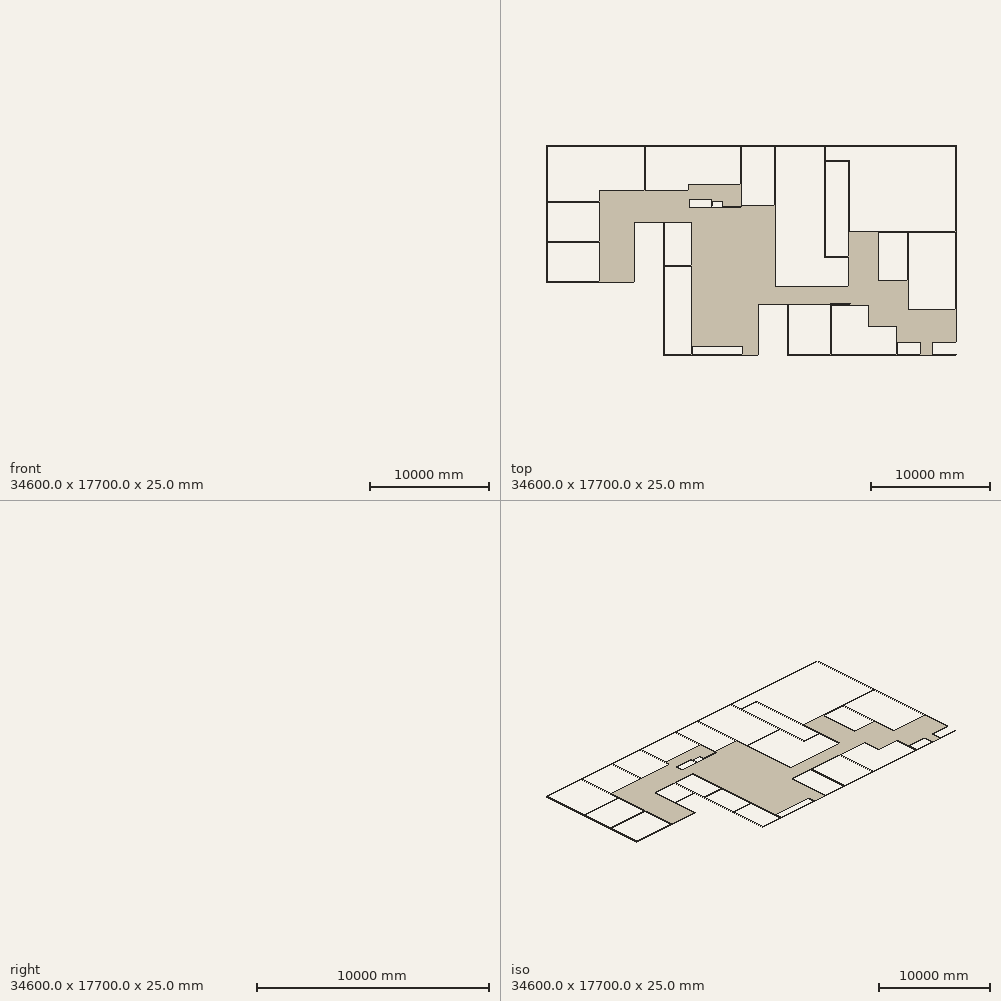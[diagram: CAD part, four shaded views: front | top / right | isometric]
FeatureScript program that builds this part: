
annotation { "Feature Type Name" : "Feature", "Feature Type Description" : "" }
export const myFeature = defineFeature(function(context is Context, id is Id, definition is map)
    precondition{}
    {
        {
            var Q0;
            Q0=qCreatedBy(makeId("Top.planeOp"),FACE);
            var sketch = newSketch(context, id + "F0", { "sketchPlane" : qUnion([Q0])});
            skLineSegment(sketch, "E0", {"start": v(-12169.64, -2200) * mm, "end": v(-12169.64, 9350) * mm});
            skLineSegment(sketch, "E1", {"start": v(-12169.64, 9350) * mm, "end": v(22430.36, 9350) * mm});
            skLineSegment(sketch, "E2", {"start": v(22430.36, 9350) * mm, "end": v(22430.36, -8350) * mm});
            skLineSegment(sketch, "E3", {"start": v(22430.36, -8350) * mm, "end": v(-2269.64, -8350) * mm});
            skLineSegment(sketch, "E4", {"start": v(-2269.64, -8350) * mm, "end": v(-2269.64, 300) * mm});
            skLineSegment(sketch, "E5", {"start": v(-2269.64, 300) * mm, "end": v(-4769.64, 300) * mm});
            skLineSegment(sketch, "E6", {"start": v(-4769.64, 300) * mm, "end": v(-4769.64, -2200) * mm});
            skLineSegment(sketch, "E7", {"start": v(-4769.64, -2200) * mm, "end": v(-12169.64, -2200) * mm});
            skLineSegment(sketch, "E8.bottom", {"start": v(-12119.64, 9300) * mm, "end": v(-7719.64, 9300) * mm});
            skLineSegment(sketch, "E8.top", {"start": v(-12119.64, 4600) * mm, "end": v(-7719.64, 4600) * mm});
            skLineSegment(sketch, "E8.left", {"start": v(-12119.64, 9300) * mm, "end": v(-12119.64, 4600) * mm});
            skLineSegment(sketch, "E8.right", {"start": v(-7719.64, 9300) * mm, "end": v(-7719.64, 4600) * mm});
            skLineSegment(sketch, "E9.bottom", {"start": v(-7669.64, 9300) * mm, "end": v(-3869.64, 9300) * mm});
            skLineSegment(sketch, "E9.top", {"start": v(-7669.64, 5600) * mm, "end": v(-3869.64, 5600) * mm});
            skLineSegment(sketch, "E9.left", {"start": v(-7669.64, 9300) * mm, "end": v(-7669.64, 5600) * mm});
            skLineSegment(sketch, "E9.right", {"start": v(-3869.64, 9300) * mm, "end": v(-3869.64, 5600) * mm});
            skLineSegment(sketch, "E10.bottom", {"start": v(-3819.64, 9300) * mm, "end": v(-219.64, 9300) * mm});
            skLineSegment(sketch, "E10.top", {"start": v(-3819.64, 5600) * mm, "end": v(-219.64, 5600) * mm});
            skLineSegment(sketch, "E10.left", {"start": v(-3819.64, 9300) * mm, "end": v(-3819.64, 5600) * mm});
            skLineSegment(sketch, "E10.right", {"start": v(-219.64, 9300) * mm, "end": v(-219.64, 5600) * mm});
            skLineSegment(sketch, "E11.bottom", {"start": v(-12119.64, 1175) * mm, "end": v(-7719.64, 1175) * mm});
            skLineSegment(sketch, "E11.top", {"start": v(-12119.64, -2150) * mm, "end": v(-7719.64, -2150) * mm});
            skLineSegment(sketch, "E11.left", {"start": v(-12119.64, 1175) * mm, "end": v(-12119.64, -2150) * mm});
            skLineSegment(sketch, "E11.right", {"start": v(-7719.64, 1175) * mm, "end": v(-7719.64, -2150) * mm});
            skLineSegment(sketch, "E12.bottom", {"start": v(-12119.64, 4550) * mm, "end": v(-7719.64, 4550) * mm});
            skLineSegment(sketch, "E12.top", {"start": v(-12119.64, 1225) * mm, "end": v(-7719.64, 1225) * mm});
            skLineSegment(sketch, "E12.left", {"start": v(-12119.64, 4550) * mm, "end": v(-12119.64, 1225) * mm});
            skLineSegment(sketch, "E12.right", {"start": v(-7719.64, 4550) * mm, "end": v(-7719.64, 1225) * mm});
            skLineSegment(sketch, "E13.bottom", {"start": v(-169.64, 9300) * mm, "end": v(4230.36, 9300) * mm});
            skLineSegment(sketch, "E13.top", {"start": v(-169.64, 6100) * mm, "end": v(4230.36, 6100) * mm});
            skLineSegment(sketch, "E13.left", {"start": v(-169.64, 9300) * mm, "end": v(-169.64, 6100) * mm});
            skLineSegment(sketch, "E13.right", {"start": v(4230.36, 9300) * mm, "end": v(4230.36, 6100) * mm});
            skLineSegment(sketch, "E14.bottom", {"start": v(4280.36, 9300) * mm, "end": v(7080.36, 9300) * mm});
            skLineSegment(sketch, "E14.top", {"start": v(4280.36, 4300) * mm, "end": v(7080.36, 4300) * mm});
            skLineSegment(sketch, "E14.left", {"start": v(4280.36, 9300) * mm, "end": v(4280.36, 4300) * mm});
            skLineSegment(sketch, "E14.right", {"start": v(7080.36, 9300) * mm, "end": v(7080.36, 4300) * mm});
            skLineSegment(sketch, "E15.bottom", {"start": v(-129.64, 4190) * mm, "end": v(4270.36, 4190) * mm});
            skLineSegment(sketch, "E15.top", {"start": v(-129.64, 4090) * mm, "end": v(4270.36, 4090) * mm});
            skLineSegment(sketch, "E15.left", {"start": v(-129.64, 4190) * mm, "end": v(-129.64, 4090) * mm});
            skLineSegment(sketch, "E15.right", {"start": v(4270.36, 4190) * mm, "end": v(4270.36, 4090) * mm});
            skLineSegment(sketch, "E16.bottom", {"start": v(-2219.64, -4600) * mm, "end": v(80.36, -4600) * mm});
            skLineSegment(sketch, "E16.top", {"start": v(-2219.64, -8300) * mm, "end": v(80.36, -8300) * mm});
            skLineSegment(sketch, "E16.left", {"start": v(-2219.64, -4600) * mm, "end": v(-2219.64, -8300) * mm});
            skLineSegment(sketch, "E16.right", {"start": v(80.36, -4600) * mm, "end": v(80.36, -8300) * mm});
            skLineSegment(sketch, "E17.bottom", {"start": v(-2219.64, -850) * mm, "end": v(80.36, -850) * mm});
            skLineSegment(sketch, "E17.top", {"start": v(-2219.64, -4550) * mm, "end": v(80.36, -4550) * mm});
            skLineSegment(sketch, "E17.left", {"start": v(-2219.64, -850) * mm, "end": v(-2219.64, -4550) * mm});
            skLineSegment(sketch, "E17.right", {"start": v(80.36, -850) * mm, "end": v(80.36, -4550) * mm});
            skLineSegment(sketch, "E18.bottom", {"start": v(-2219.64, 2900) * mm, "end": v(80.36, 2900) * mm});
            skLineSegment(sketch, "E18.top", {"start": v(-2219.64, -800) * mm, "end": v(80.36, -800) * mm});
            skLineSegment(sketch, "E18.left", {"start": v(-2219.64, 2900) * mm, "end": v(-2219.64, -800) * mm});
            skLineSegment(sketch, "E18.right", {"start": v(80.36, 2900) * mm, "end": v(80.36, -800) * mm});
            skLineSegment(sketch, "E19.bottom", {"start": v(7130.36, 9300) * mm, "end": v(11330.36, 9300) * mm});
            skLineSegment(sketch, "E19.top", {"start": v(7130.36, 3050) * mm, "end": v(11330.36, 3050) * mm});
            skLineSegment(sketch, "E19.left", {"start": v(7130.36, 9300) * mm, "end": v(7130.36, 3050) * mm});
            skLineSegment(sketch, "E19.right", {"start": v(11330.36, 9300) * mm, "end": v(11330.36, 3050) * mm});
            skLineSegment(sketch, "E20", {"start": v(11380.36, 9300) * mm, "end": v(22380.36, 9300) * mm});
            skLineSegment(sketch, "E21", {"start": v(22380.36, 9300) * mm, "end": v(22380.36, 2100) * mm});
            skLineSegment(sketch, "E22", {"start": v(13380.36, 8100) * mm, "end": v(11380.36, 8100) * mm});
            skLineSegment(sketch, "E23", {"start": v(11380.36, 8100) * mm, "end": v(11380.36, 9300) * mm});
            skLineSegment(sketch, "E24.bottom", {"start": v(11380.36, 8050) * mm, "end": v(13330.36, 8050) * mm});
            skLineSegment(sketch, "E24.left", {"start": v(11380.36, 8050) * mm, "end": v(11380.36, 0) * mm});
            skLineSegment(sketch, "E24.right", {"start": v(13330.36, 8050) * mm, "end": v(13330.36, 0) * mm});
            skLineSegment(sketch, "E25", {"start": v(13380.36, -2550) * mm, "end": v(13480.36, -2550) * mm});
            skLineSegment(sketch, "E26", {"start": v(13480.36, -2550) * mm, "end": v(13480.36, -4050) * mm});
            skLineSegment(sketch, "E27", {"start": v(13480.36, -4050) * mm, "end": v(11880.36, -4050) * mm});
            skLineSegment(sketch, "E28.bottom", {"start": v(8230.36, -4050) * mm, "end": v(11830.36, -4050) * mm});
            skLineSegment(sketch, "E28.top", {"start": v(8230.36, -8300) * mm, "end": v(11830.36, -8300) * mm});
            skLineSegment(sketch, "E28.left", {"start": v(8230.36, -4050) * mm, "end": v(8230.36, -8300) * mm});
            skLineSegment(sketch, "E28.right", {"start": v(11830.36, -4050) * mm, "end": v(11830.36, -8300) * mm});
            skLineSegment(sketch, "E29.right", {"start": v(13330.36, -50) * mm, "end": v(13330.36, -2550) * mm});
            skLineSegment(sketch, "E30", {"start": v(7130.36, 3000) * mm, "end": v(7130.36, -2550) * mm});
            skLineSegment(sketch, "E31", {"start": v(11330.36, 3000) * mm, "end": v(7130.36, 3000) * mm});
            skLineSegment(sketch, "E32", {"start": v(11380.36, 0) * mm, "end": v(13330.36, 0) * mm});
            skLineSegment(sketch, "E33.bottom", {"start": v(5741.05, -4050) * mm, "end": v(8141.05, -4050) * mm});
            skLineSegment(sketch, "E33.top", {"start": v(5741.05, -8340) * mm, "end": v(8141.05, -8340) * mm});
            skLineSegment(sketch, "E33.left", {"start": v(5741.05, -4050) * mm, "end": v(5741.05, -8340) * mm});
            skLineSegment(sketch, "E33.right", {"start": v(8141.05, -4050) * mm, "end": v(8141.05, -8340) * mm});
            skLineSegment(sketch, "E34", {"start": v(13380.36, -2550) * mm, "end": v(13380.36, 2050) * mm});
            skLineSegment(sketch, "E35", {"start": v(13380.36, 2050) * mm, "end": v(14748.13, 2050) * mm});
            skLineSegment(sketch, "E36", {"start": v(15830.36, -2000) * mm, "end": v(18330.36, -2000) * mm});
            skLineSegment(sketch, "E37", {"start": v(18380.36, 2050) * mm, "end": v(18380.36, -4450) * mm});
            skLineSegment(sketch, "E38", {"start": v(18380.36, -4450) * mm, "end": v(22380.36, -4450) * mm});
            skLineSegment(sketch, "E39", {"start": v(22380.36, -4450) * mm, "end": v(22380.36, 2050) * mm});
            skLineSegment(sketch, "E40", {"start": v(22380.36, 2050) * mm, "end": v(18380.36, 2050) * mm});
            skLineSegment(sketch, "E41", {"start": v(14748.13, 2050) * mm, "end": v(18380.36, 2050) * mm});
            skLineSegment(sketch, "E42", {"start": v(15830.36, -2000) * mm, "end": v(15830.36, 2000) * mm});
            skLineSegment(sketch, "E43", {"start": v(15830.36, 2000) * mm, "end": v(18330.36, 2000) * mm});
            skLineSegment(sketch, "E44", {"start": v(18330.36, 2000) * mm, "end": v(18330.36, -2000) * mm});
            skLineSegment(sketch, "E45.bottom", {"start": v(18430.36, 2000) * mm, "end": v(22330.36, 2000) * mm});
            skLineSegment(sketch, "E45.top", {"start": v(18430.36, -4400) * mm, "end": v(22330.36, -4400) * mm});
            skLineSegment(sketch, "E45.left", {"start": v(18430.36, 2000) * mm, "end": v(18430.36, -4400) * mm});
            skLineSegment(sketch, "E45.right", {"start": v(22330.36, 2000) * mm, "end": v(22330.36, -4400) * mm});
            skLineSegment(sketch, "E46", {"start": v(11880.36, -8300) * mm, "end": v(11880.36, -4100) * mm});
            skLineSegment(sketch, "E47", {"start": v(11880.36, -4100) * mm, "end": v(15010.36, -4100) * mm});
            skLineSegment(sketch, "E48", {"start": v(15010.36, -4100) * mm, "end": v(15010.36, -5880) * mm});
            skLineSegment(sketch, "E49", {"start": v(15010.36, -5880) * mm, "end": v(17360.36, -5880) * mm});
            skLineSegment(sketch, "E50", {"start": v(17360.36, -5880) * mm, "end": v(17360.36, -8300) * mm});
            skLineSegment(sketch, "E51", {"start": v(17360.36, -8300) * mm, "end": v(11880.36, -8300) * mm});
            skLineSegment(sketch, "E52", {"start": v(11930.36, -8250) * mm, "end": v(17310.36, -8250) * mm});
            skLineSegment(sketch, "E53", {"start": v(17310.36, -8250) * mm, "end": v(17310.36, -5930) * mm});
            skLineSegment(sketch, "E54", {"start": v(17310.36, -5930) * mm, "end": v(14960.36, -5930) * mm});
            skLineSegment(sketch, "E55", {"start": v(14960.36, -5930) * mm, "end": v(14960.36, -4150) * mm});
            skLineSegment(sketch, "E56", {"start": v(11930.36, -8250) * mm, "end": v(11930.36, -4150) * mm});
            skLineSegment(sketch, "E57", {"start": v(11930.36, -4150) * mm, "end": v(14960.36, -4150) * mm});
            skLineSegment(sketch, "E58", {"start": v(11330.36, 3000) * mm, "end": v(11330.36, -50) * mm});
            skLineSegment(sketch, "E59", {"start": v(11330.36, -50) * mm, "end": v(13330.36, -50) * mm});
            skLineSegment(sketch, "E60", {"start": v(7180.36, 2950) * mm, "end": v(7180.36, -2500) * mm});
            skLineSegment(sketch, "E61", {"start": v(7180.36, -2500) * mm, "end": v(13280.36, -2500) * mm});
            skLineSegment(sketch, "E62", {"start": v(13280.36, -2500) * mm, "end": v(13280.36, -123.09) * mm});
            skLineSegment(sketch, "E63", {"start": v(13280.36, -123.09) * mm, "end": v(11280.36, -123.09) * mm});
            skLineSegment(sketch, "E64", {"start": v(7180.36, 2950) * mm, "end": v(11280.36, 2950) * mm});
            skLineSegment(sketch, "E65", {"start": v(11280.36, 2950) * mm, "end": v(11280.36, -123.09) * mm});
            skLineSegment(sketch, "E66", {"start": v(7130.36, -2550) * mm, "end": v(13330.36, -2550) * mm});
            skLineSegment(sketch, "E67", {"start": v(11835.32, -4008.48) * mm, "end": v(11835.32, -4030.26) * mm});
            skLineSegment(sketch, "E68", {"start": v(11835.32, -4030.26) * mm, "end": v(13457.04, -4030.26) * mm});
            skLineSegment(sketch, "E69", {"start": v(13457.04, -4030.26) * mm, "end": v(13457.04, -4008.48) * mm});
            skLineSegment(sketch, "E70", {"start": v(13457.04, -4008.48) * mm, "end": v(11835.32, -4008.48) * mm});
            skLineSegment(sketch, "E71", {"start": v(13380.36, 8100) * mm, "end": v(13380.36, 2100) * mm});
            skLineSegment(sketch, "E72", {"start": v(13380.36, 2100) * mm, "end": v(22380.36, 2100) * mm});
            skLineSegment(sketch, "E73.bottom", {"start": v(17410.36, -7300) * mm, "end": v(19410.36, -7300) * mm});
            skLineSegment(sketch, "E73.top", {"start": v(17410.36, -8300) * mm, "end": v(19410.36, -8300) * mm});
            skLineSegment(sketch, "E73.left", {"start": v(17410.36, -7300) * mm, "end": v(17410.36, -8300) * mm});
            skLineSegment(sketch, "E73.right", {"start": v(19410.36, -7300) * mm, "end": v(19410.36, -8300) * mm});
            skLineSegment(sketch, "E74.bottom", {"start": v(20410.36, -7300) * mm, "end": v(22410.36, -7300) * mm});
            skLineSegment(sketch, "E74.top", {"start": v(20410.36, -8300) * mm, "end": v(22410.36, -8300) * mm});
            skLineSegment(sketch, "E74.left", {"start": v(20410.36, -7300) * mm, "end": v(20410.36, -8300) * mm});
            skLineSegment(sketch, "E74.right", {"start": v(22410.36, -7300) * mm, "end": v(22410.36, -8300) * mm});
            skLineSegment(sketch, "E75.bottom", {"start": v(130.36, -7600) * mm, "end": v(4330.36, -7600) * mm});
            skLineSegment(sketch, "E75.top", {"start": v(130.36, -8300) * mm, "end": v(4330.36, -8300) * mm});
            skLineSegment(sketch, "E75.left", {"start": v(130.36, -7600) * mm, "end": v(130.36, -8300) * mm});
            skLineSegment(sketch, "E75.right", {"start": v(4330.36, -7600) * mm, "end": v(4330.36, -8300) * mm});
            skLineSegment(sketch, "E76.bottom", {"start": v(-129.64, 4821) * mm, "end": v(1770.36, 4821) * mm});
            skLineSegment(sketch, "E76.top", {"start": v(-129.64, 4191) * mm, "end": v(1770.36, 4191) * mm});
            skLineSegment(sketch, "E76.left", {"start": v(-129.64, 4821) * mm, "end": v(-129.64, 4191) * mm});
            skLineSegment(sketch, "E76.right", {"start": v(1770.36, 4821) * mm, "end": v(1770.36, 4191) * mm});
            skLineSegment(sketch, "E77.bottom", {"start": v(1820.36, 4641) * mm, "end": v(2720.36, 4641) * mm});
            skLineSegment(sketch, "E77.top", {"start": v(1820.36, 4191) * mm, "end": v(2720.36, 4191) * mm});
            skLineSegment(sketch, "E77.left", {"start": v(1820.36, 4641) * mm, "end": v(1820.36, 4191) * mm});
            skLineSegment(sketch, "E77.right", {"start": v(2720.36, 4641) * mm, "end": v(2720.36, 4191) * mm});
            skLineSegment(sketch, "E78.bottom", {"start": v(-2269.64, 2900) * mm, "end": v(-4769.64, 2900) * mm});
            skLineSegment(sketch, "E78.top", {"start": v(-2269.64, 350) * mm, "end": v(-4769.64, 350) * mm});
            skLineSegment(sketch, "E78.left", {"start": v(-2269.64, 2900) * mm, "end": v(-2269.64, 350) * mm});
            skLineSegment(sketch, "E78.right", {"start": v(-4769.64, 2900) * mm, "end": v(-4769.64, 350) * mm});
            skSolve(sketch);
        }
        {
            var Q0;
            Q0 = qSketchRegion(id + "F0", true);
            extrude(context, id + "F1", {"entities" : qUnion([Q0]), "depth" : 25 * mm, "offsetDistance" : 25 * mm});
        }
    });
